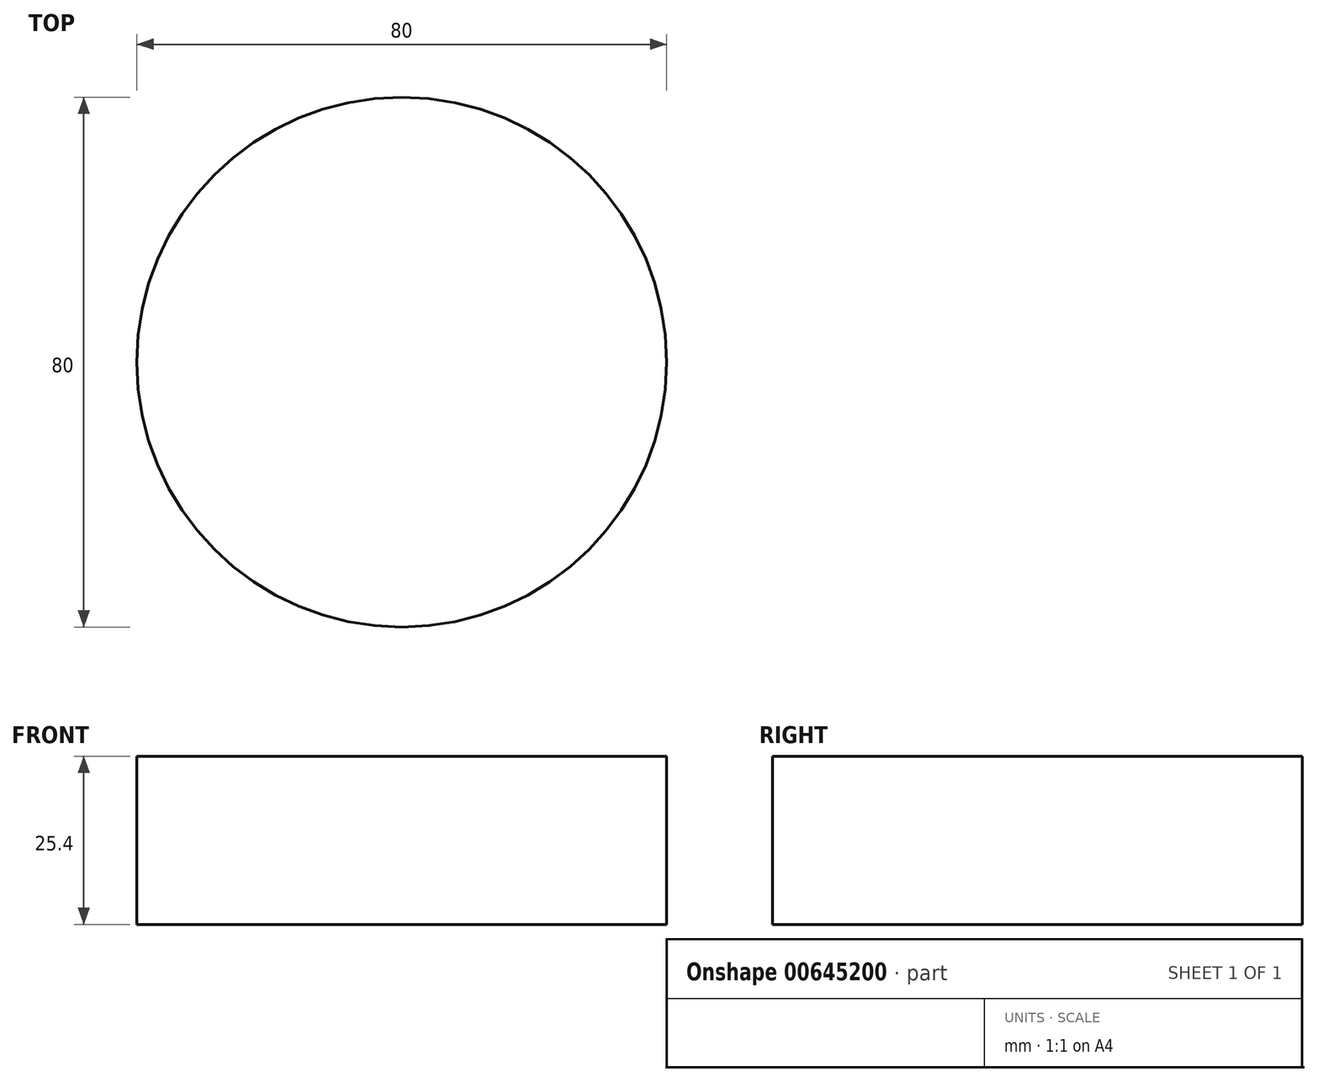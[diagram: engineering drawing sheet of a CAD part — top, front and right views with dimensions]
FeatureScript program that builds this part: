
annotation { "Feature Type Name" : "Feature", "Feature Type Description" : "" }
export const myFeature = defineFeature(function(context is Context, id is Id, definition is map)
    precondition{}
    {
        {
            var Q0;
            Q0=qCreatedBy(makeId("Top.planeOp"),FACE);
            var sketch = newSketch(context, id + "F0", { "sketchPlane" : qUnion([Q0])});
            skCircle(sketch, "E0", {"center": v(-24.11, 32.56) * mm, "radius": 40 * mm});
            skSolve(sketch);
        }
        {
            var Q0;
            Q0=makeQuery(id+"F0.imprint","IMPRINT",FACE,{"disambiguationData":[TD([[makeQuery(id+"F0.imprint","IMPRINT",EDGE,{"derivedFrom":sQuery(id+"F0.wireOp",EDGE,"E0")}),1.0]])]});
            extrude(context, id + "F1", {"entities" : qUnion([Q0]), "depth" : 25.4 * mm, "offsetDistance" : 25.4 * mm});
        }
    });
